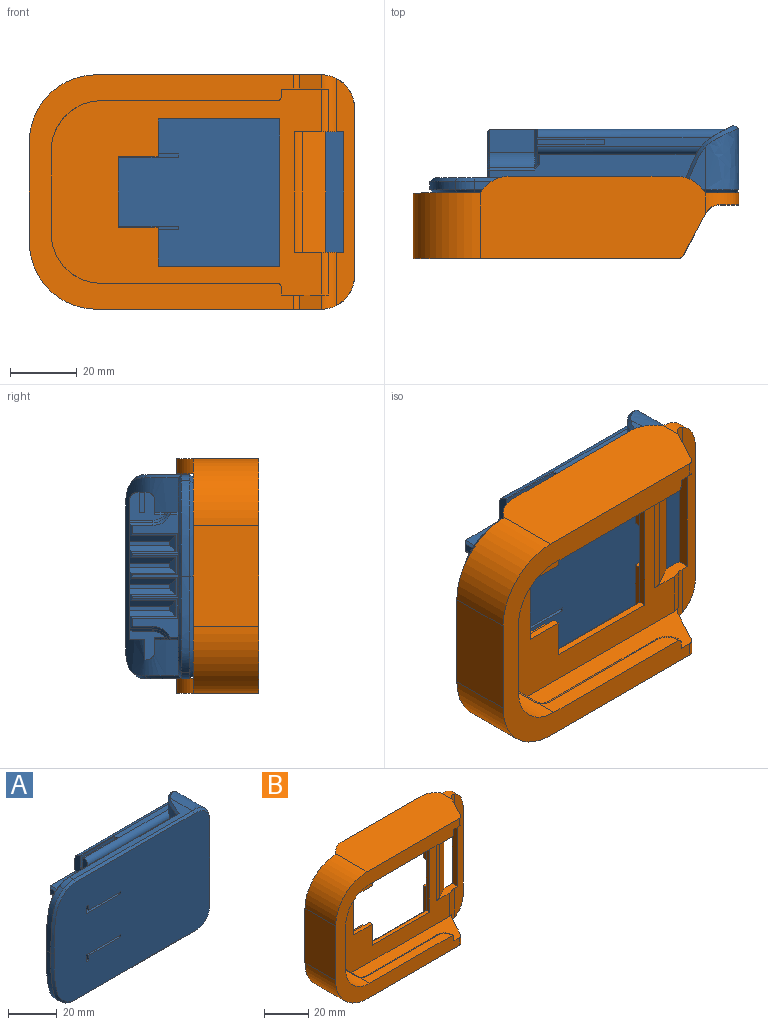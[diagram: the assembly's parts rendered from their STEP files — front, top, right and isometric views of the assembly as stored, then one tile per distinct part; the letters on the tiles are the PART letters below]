
ASSEMBLY  parts=2 mates=1
PART A: 135 faces, bbox 93.4x24.2x62.2 mm
  f0: plane 91.38x60.19mm, normal (0,-1,0), area 5145.7mm2, adj f1,f102,f103,f104,f105,f106,f107,f108
  f1: plane 18.5x16.5mm, normal (0,0,1), area 305.3mm2, adj f0,f122,f124,f134
  f2: plane 13x12mm, normal (0,0,1), area 37.3mm2, adj f6,f24,f25,f39,f122,f123
  f3: plane 61.69x7.04mm, normal (0,0,-1), area 352.6mm2, adj f8,f15,f19,f85,f86,f88,f99
  f4: plane 61.69x7.04mm, normal (0,0,1), area 352.6mm2, adj f9,f15,f18,f69,f72,f75,f99
  f5: plane 49.52x0.5mm, normal (0,0,-1), area 24.6mm2, adj f10,f12,f55,f99
  f6: plane 70.51x41.5mm, normal (0,1,0), area 2710mm2, adj f2,f11,f14,f23,f24,f26,f27,f28
  f7: plane 51.92x2.54mm, normal (0,0,1), area 95.9mm2, adj f13,f14,f20,f22,f50,f53,f99
  f8: plane 47.42x4.25mm, normal (0,-1,0), area 166.2mm2, adj f3,f12,f55,f86,f99
  f9: plane 47.42x4.25mm, normal (0,-1,0), area 166.2mm2, adj f4,f13,f53,f69,f99
  f10: plane 49.51x6mm, normal (0,1,0), area 297.1mm2, adj f5,f11,f55,f99
  f11: plane 56.3x4.58mm, normal (0,0,-1), area 236.2mm2, adj f6,f10,f55,f99
  f12: cylinder r=2.5mm len=49.08mm, axis (1,0,0), area 189.5mm2, adj f5,f8,f55,f99
  f13: cylinder r=2.5mm len=49.08mm, axis (-1,0,0), area 189.5mm2, adj f7,f9,f53,f99
  f14: cylinder r=2.5mm len=56.26mm, axis (-1,0,0), area 212.4mm2, adj f6,f7,f53,f99
  f15: plane 76.68x60.17mm, normal (0,1,0), area 2097.9mm2, adj f3,f4,f16,f18,f19,f99,f111,f112
  f16: plane 36.5x13.75mm, normal (-1,0,0), area 123.2mm2, adj f15,f18,f19,f57,f58,f59,f60,f61
  f17: plane 41x18.31mm, normal (1,0,0), area 750.7mm2, adj f100,f101,f102,f118
  f18: plane 2.37x0.75mm, normal (-0.71,0,0.71), area 2.5mm2, adj f4,f15,f16,f77
  f19: plane 2.37x0.75mm, normal (-0.71,0,-0.71), area 2.5mm2, adj f3,f15,f16,f82
  f20: plane 20x6mm, normal (0,-1,0), area 120mm2, adj f7,f21,f50,f53
  f21: plane 20x1.5mm, normal (0,0,1), area 30mm2, adj f20,f22,f50,f53
  f22: plane 20x6mm, normal (0,1,0), area 120mm2, adj f7,f21,f50,f53
  f23: plane 13x12mm, normal (0,0,-1), area 156mm2, adj f6,f24,f25,f38
  f24: plane 12x1.2mm, normal (-1,0,0), area 14.4mm2, adj f2,f6,f23,f25,f125
  f25: plane 13x1.2mm, normal (0,1,0), area 15.6mm2, adj f2,f23,f24,f40,f125
  f26: plane 13x12mm, normal (0,0,1), area 156mm2, adj f6,f28,f29,f42
  f27: plane 13x12mm, normal (0,0,-1), area 156mm2, adj f6,f28,f29,f41
  f28: plane 12x1.2mm, normal (-1,0,0), area 14.4mm2, adj f6,f26,f27,f29
  f29: plane 13x1.2mm, normal (0,1,0), area 15.6mm2, adj f26,f27,f28,f43
  f30: plane 13x12mm, normal (0,0,1), area 156mm2, adj f6,f32,f33,f45
  f31: plane 13x12mm, normal (0,0,-1), area 156mm2, adj f6,f32,f33,f44
  f32: plane 12x1.2mm, normal (-1,0,0), area 14.4mm2, adj f6,f30,f31,f33
  f33: plane 13x1.2mm, normal (0,1,0), area 15.6mm2, adj f30,f31,f32,f46
  f34: plane 13x12mm, normal (0,0,-1), area 37.3mm2, adj f6,f35,f37,f47,f127,f128
  f35: plane 12x1.2mm, normal (-1,0,0), area 14.4mm2, adj f6,f34,f36,f37,f126
  f36: plane 13x12mm, normal (0,0,1), area 156mm2, adj f6,f35,f37,f48
  f37: plane 13x1.2mm, normal (0,1,0), area 15.6mm2, adj f34,f35,f36,f49,f126
  f38: plane 13.78x1.78mm, normal (-0.71,0,-0.71), area 32.3mm2, adj f6,f23,f40,f76,f78
  f39: plane 13.78x1.78mm, normal (-0.71,0,0.71), area 32.3mm2, adj f2,f6,f40,f80,f81
  f40: plane 4.76x1.78mm, normal (-0.71,0.71,0), area 7.5mm2, adj f25,f38,f39,f79
  f41: plane 13.78x1.78mm, normal (-0.71,0,-0.71), area 32.3mm2, adj f6,f27,f43,f63,f66
  f42: plane 13.78x1.78mm, normal (-0.71,0,0.71), area 32.3mm2, adj f6,f26,f43,f73,f76
  f43: plane 4.76x1.78mm, normal (-0.71,0.71,0), area 7.5mm2, adj f29,f41,f42,f70
  f44: plane 13.78x1.78mm, normal (-0.71,0,-0.71), area 32.3mm2, adj f6,f31,f46,f57,f58
  f45: plane 13.78x1.78mm, normal (-0.71,0,0.71), area 32.3mm2, adj f6,f30,f46,f61,f63
  f46: plane 4.76x1.78mm, normal (-0.71,0.71,0), area 7.5mm2, adj f33,f44,f45,f59
  f47: plane 13.78x1.78mm, normal (-0.71,0,-0.71), area 32.3mm2, adj f6,f34,f49,f64,f67
  f48: plane 13.78x1.78mm, normal (-0.71,0,0.71), area 32.3mm2, adj f6,f36,f49,f58,f60
  f49: plane 4.76x1.78mm, normal (-0.71,0.71,0), area 7.5mm2, adj f37,f47,f48,f62
  f50: plane 6x1.5mm, normal (-1,0,0), area 9mm2, adj f7,f20,f21,f22
  f51: cylinder r=5mm len=13.5mm, axis (-1,0,0), area 74.4mm2, adj f52,f68,f74,f75
  f52: plane 13.5x7mm, normal (0,0,1), area 94.5mm2, adj f6,f51,f65,f71
  f53: plane 10.36x8.4mm, normal (-1,0,0), area 54.4mm2, adj f6,f7,f9,f13,f14,f20,f21,f22
  f54: cylinder r=5mm len=13.5mm, axis (-1,0,0), area 74.2mm2, adj f84,f85,f89,f90
  f55: plane 10.36x8.57mm, normal (-1,0,0), area 38.3mm2, adj f5,f6,f8,f10,f11,f12,f86,f90
  f56: plane 13.5x6.99mm, normal (0,0.02,-1), area 94.4mm2, adj f6,f83,f89,f92
  f57: plane 13.78x0.53mm, normal (-0.92,0,-0.38), area 7.7mm2, adj f16,f44,f58,f59
  f58: plane 2.8x0.75mm, normal (-0.71,0.71,0), area 2.1mm2, adj f6,f16,f44,f48,f57,f60
  f59: plane 5.82x0.53mm, normal (-0.92,0.38,0), area 3mm2, adj f16,f46,f57,f61
  f60: plane 13.78x0.53mm, normal (-0.92,0,0.38), area 7.7mm2, adj f16,f48,f58,f62
  f61: plane 13.78x0.53mm, normal (-0.92,0,0.38), area 7.7mm2, adj f16,f45,f59,f63
  f62: plane 5.82x0.53mm, normal (-0.92,0.38,0), area 3mm2, adj f16,f49,f60,f64
  f63: plane 2.8x0.75mm, normal (-0.71,0.71,0), area 2.1mm2, adj f6,f16,f41,f45,f61,f66
  f64: plane 13.78x0.53mm, normal (-0.92,0,-0.38), area 7.7mm2, adj f16,f47,f62,f67
  f65: plane 7x0.75mm, normal (-0.71,0,0.71), area 7.4mm2, adj f6,f52,f53,f68
  f66: plane 13.78x0.53mm, normal (-0.92,0,-0.38), area 7.7mm2, adj f16,f41,f63,f70
  f67: plane 4.25x0.75mm, normal (-0.71,0.71,0), area 3.7mm2, adj f6,f16,f47,f64,f71
  f68: cone r=4.25mm half-angle=45deg, axis (-1,0,0), area 5mm2, adj f51,f53,f65,f72
  f69: plane 2.86x0.75mm, normal (-0.71,0,0.71), area 3mm2, adj f4,f9,f53,f72
  f70: plane 5.82x0.53mm, normal (-0.92,0.38,0), area 3mm2, adj f16,f43,f66,f73
  f71: plane 7x0.75mm, normal (-0.71,0,0.71), area 7mm2, adj f16,f52,f67,f74
  f72: bspline ~1.77x1.5mm, area 1.4mm2, adj f4,f68,f69,f75
  f73: plane 13.78x0.53mm, normal (-0.92,0,0.38), area 7.7mm2, adj f16,f42,f70,f76
  f74: cone r=5mm half-angle=45deg, axis (-1,0,0), area 6.3mm2, adj f16,f51,f71,f77
  f75: plane 13.5x0.67mm, normal (0,0.52,0.85), area 10.6mm2, adj f4,f51,f72,f77
  f76: plane 2.8x0.75mm, normal (-0.71,0.71,0), area 2.1mm2, adj f6,f16,f38,f42,f73,f78
  f77: plane 0.75x0.75mm, normal (-0.65,0.4,0.65), area 0.4mm2, adj f18,f74,f75
  f78: plane 13.78x0.53mm, normal (-0.92,0,-0.38), area 7.7mm2, adj f16,f38,f76,f79
  f79: plane 5.82x0.53mm, normal (-0.92,0.38,0), area 3mm2, adj f16,f40,f78,f80
  f80: plane 13.78x0.53mm, normal (-0.92,0,0.38), area 7.7mm2, adj f16,f39,f79,f81
  f81: plane 4.08x0.75mm, normal (-0.71,0.71,0), area 3.5mm2, adj f6,f16,f39,f80,f83
  f82: plane 0.75x0.75mm, normal (-0.65,0.4,-0.65), area 0.4mm2, adj f19,f84,f85
  f83: plane 7.01x0.91mm, normal (-0.71,0.02,-0.71), area 7mm2, adj f16,f56,f81,f87
  f84: cone r=5.75mm half-angle=45deg, axis (-1,0,0), area 6.3mm2, adj f16,f54,f82,f87
  f85: plane 13.5x0.67mm, normal (0,0.52,-0.85), area 10.6mm2, adj f3,f54,f82,f88
  f86: plane 2.86x0.75mm, normal (-0.71,0,-0.71), area 3mm2, adj f3,f8,f55,f88
  f87: plane 0.75x0.75mm, normal (-0.71,0.01,-0.71), area 0mm2, adj f83,f84,f89
  f88: bspline ~1.77x1.5mm, area 1.4mm2, adj f3,f85,f86,f90
  f89: plane 13.5x0.02mm, normal (0,0.01,-1), area 0.2mm2, adj f54,f56,f87,f91
  f90: cone r=5mm half-angle=45deg, axis (-1,0,0), area 4.9mm2, adj f54,f55,f88,f91
  f91: plane 0.75x0.75mm, normal (-0.71,0.01,-0.71), area 0mm2, adj f55,f89,f90,f92
  f92: plane 6.99x0.92mm, normal (-0.71,0.02,-0.71), area 7.4mm2, adj f6,f55,f56,f91
  f93: plane 69.47x13.29mm, normal (0,0,1), area 200.8mm2, adj f97,f101,f106,f112,f114
  f94: extruded ~28.63x7.5mm, area 77.3mm2, adj f95,f97,f110,f113
  f95: extruded ~28.63x7.5mm, area 77.3mm2, adj f94,f98,f109,f115
  f96: plane 69.47x13.29mm, normal (0,0,-1), area 200.8mm2, adj f98,f100,f105,f119,f121
  f97: cylinder r=10mm len=5.83mm, axis (0,1,0), area 15.6mm2, adj f93,f94,f108,f111
  f98: cylinder r=10mm len=5.83mm, axis (0,1,0), area 15.6mm2, adj f95,f96,f107,f117
  f99: extruded ~59x15.71mm, area 451mm2, adj f3,f4,f5,f6,f7,f8,f9,f10
  f100: bspline ~23.01x10mm, area 251.8mm2, adj f17,f96,f103,f120
  f101: bspline ~23.01x10mm, area 251.8mm2, adj f17,f93,f104,f116
  f102: plane 41x1mm, normal (0.71,-0.71,0), area 58mm2, adj f0,f17,f103,f104
  f103: bspline ~10.01x10mm, area 21.9mm2, adj f0,f100,f102,f105
  f104: bspline ~10.01x10mm, area 21.9mm2, adj f0,f101,f102,f106
  f105: plane 68.84x1mm, normal (0,-0.71,-0.71), area 97.3mm2, adj f0,f96,f103,f107
  f106: plane 68.84x1mm, normal (0,-0.71,0.71), area 97.3mm2, adj f0,f93,f104,f108
  f107: cone r=9mm half-angle=45deg, axis (0,1,0), area 8.4mm2, adj f0,f98,f105,f109
  f108: cone r=9mm half-angle=45deg, axis (0,1,0), area 8.4mm2, adj f0,f97,f106,f110
  f109: bspline ~30.14x8.1mm, area 43mm2, adj f0,f95,f107,f110
  f110: bspline ~30.14x8.1mm, area 43mm2, adj f0,f94,f108,f109
  f111: cone r=9mm half-angle=45deg, axis (0,-1,0), area 8.4mm2, adj f15,f97,f112,f113
  f112: plane 63.82x1.01mm, normal (0,0.71,0.71), area 89.8mm2, adj f15,f93,f111,f114
  f113: bspline ~30.14x8.1mm, area 43mm2, adj f15,f94,f111,f115
  f114: bspline ~10.83x5.94mm, area 15.9mm2, adj f93,f99,f112,f116
  f115: bspline ~30.14x8.1mm, area 43mm2, adj f15,f95,f113,f117
  f116: bspline ~10.75x10mm, area 27.1mm2, adj f99,f101,f114,f118
  f117: cone r=9mm half-angle=45deg, axis (0,-1,0), area 8.4mm2, adj f15,f98,f115,f119
  f118: plane 41x1.44mm, normal (0.53,0.85,0), area 69.7mm2, adj f17,f99,f116,f120
  f119: plane 63.82x1.01mm, normal (0,0.71,-0.71), area 89.8mm2, adj f15,f96,f117,f121
  f120: bspline ~10.75x10mm, area 27.1mm2, adj f99,f100,f118,f121
  f121: bspline ~11.34x6.17mm, area 15.9mm2, adj f96,f99,f119,f120
  f122: plane 20x3.5mm, normal (0,-1,0), area 23.8mm2, adj f1,f2,f123,f124,f125,f133,f134
  f123: plane 16.5x3.5mm, normal (1,0,0), area 57.8mm2, adj f0,f2,f122,f125,f133
  f124: plane 16.5x1mm, normal (-1,0,0), area 16.5mm2, adj f0,f1,f122,f125
  f125: plane 20x16.5mm, normal (0,0,-1), area 211.2mm2, adj f0,f24,f25,f122,f123,f124
  f126: plane 20x16.5mm, normal (0,0,1), area 211.3mm2, adj f0,f35,f37,f127,f128,f129
  f127: plane 16.5x3.5mm, normal (1,0,0), area 57.7mm2, adj f0,f34,f126,f128,f131
  f128: plane 20x3.5mm, normal (0,-1,0), area 23.7mm2, adj f34,f126,f127,f129,f130,f131,f132
  f129: plane 16.5x1mm, normal (-1,0,0), area 16.5mm2, adj f0,f126,f128,f130
  f130: plane 18.5x16.5mm, normal (0,0,-1), area 305.2mm2, adj f0,f128,f129,f132
  f131: plane 16.5x1.5mm, normal (0,0,-1), area 24.7mm2, adj f0,f127,f128,f132
  f132: plane 16.5x2.5mm, normal (-1,0,0), area 41.3mm2, adj f0,f128,f130,f131
  f133: plane 16.5x1.5mm, normal (0,0,1), area 24.7mm2, adj f0,f122,f123,f134
  f134: plane 16.5x2.5mm, normal (-1,0,0), area 41.2mm2, adj f0,f1,f122,f133
PART B: 83 faces, bbox 97.1x24.5x70 mm
  f0: plane 29.99x19.5mm, normal (-1,0,0), area 584.8mm2, adj f1,f4,f9,f44
  f1: cylinder r=20mm len=20mm, axis (0,-1,0), area 612.6mm2, adj f0,f4,f9,f10
  f2: plane 14.8x4.5mm, normal (0,0,1), area 38.3mm2, adj f3,f4,f6,f54,f55,f58,f61,f74
  f3: plane 80.77x61.5mm, normal (0,-1,0), area 2617.9mm2, adj f2,f7,f8,f27,f28,f29,f30,f31
  f4: plane 97.09x69.99mm, normal (0,1,0), area 3587.8mm2, adj f0,f1,f2,f12,f13,f14,f15,f16
  f5: plane 12.29x6.56mm, normal (0.88,-0.47,0), area 59.2mm2, adj f8,f11,f13,f52,f59
  f6: plane 67.82x5.47mm, normal (0,-1,0), area 263.1mm2, adj f2,f12,f13,f14,f53,f54,f58,f59
  f7: plane 67.27x15.51mm, normal (0,0,1), area 626.1mm2, adj f3,f9,f40,f41,f43,f47,f48,f50
  f8: plane 67.31x15.5mm, normal (0,0,-1), area 626.6mm2, adj f3,f5,f9,f36,f37,f39,f46,f49
  f9: plane 78.89x69.99mm, normal (0,-1,0), area 1474.1mm2, adj f0,f1,f7,f8,f10,f11,f37,f38
  f10: plane 67.09x24.5mm, normal (0,0,-1), area 1572.3mm2, adj f1,f9,f12,f50,f51,f78,f79,f80
  f11: plane 67.09x24.5mm, normal (0,0,1), area 1572.3mm2, adj f5,f9,f13,f44,f52,f76,f81,f82
  f12: cylinder r=10mm len=10mm, axis (0,1,0), area 58.7mm2, adj f4,f6,f10,f14,f50,f58
  f13: cylinder r=10mm len=10mm, axis (0,-1,0), area 58.7mm2, adj f4,f5,f6,f11,f14,f59
  f14: plane 49.99x3.5mm, normal (1,0,0), area 175mm2, adj f4,f6,f12,f13
  f15: plane 19.05x2.5mm, normal (-1,0,0), area 47.6mm2, adj f4,f16,f26,f35
  f16: plane 2.5x1.78mm, normal (0,0,-1), area 4.4mm2, adj f4,f15,f17,f35
  f17: plane 15.24x2.5mm, normal (-1,0,0), area 38.1mm2, adj f4,f16,f18,f35
  f18: plane 2.5x1.78mm, normal (0,0,1), area 4.4mm2, adj f4,f17,f19,f35
  f19: plane 14.48x2.5mm, normal (-1,0,0), area 36.2mm2, adj f4,f18,f20,f35
  f20: plane 38.35x2.5mm, normal (0,0,1), area 95.9mm2, adj f4,f19,f21,f35
  f21: plane 12.07x2.5mm, normal (1,0,0), area 30.2mm2, adj f4,f20,f22,f35
  f22: plane 12.07x2.5mm, normal (0,0,1), area 30.2mm2, adj f4,f21,f23,f35
  f23: plane 24.64x2.5mm, normal (1,0,0), area 61.6mm2, adj f4,f22,f24,f35
  f24: plane 12.07x2.5mm, normal (0,0,-1), area 30.2mm2, adj f4,f23,f25,f35
  f25: plane 12.07x2.5mm, normal (1,0,0), area 30.2mm2, adj f4,f24,f26,f35
  f26: plane 38.35x2.5mm, normal (0,0,-1), area 95.9mm2, adj f4,f15,f25,f35
  f27: plane 21.08x2mm, normal (1,0,0), area 42.2mm2, adj f3,f28,f34,f35
  f28: plane 11.94x2mm, normal (0,0,-1), area 23.9mm2, adj f3,f27,f29,f35
  f29: plane 11.26x2mm, normal (1,0,0), area 22.5mm2, adj f3,f28,f30,f35
  f30: plane 36.32x2mm, normal (0,0,-1), area 72.6mm2, adj f3,f29,f31,f35
  f31: plane 43.94x2mm, normal (-1,0,0), area 87.9mm2, adj f3,f30,f32,f35
  f32: plane 36.32x2mm, normal (0,0,1), area 72.6mm2, adj f3,f31,f33,f35
  f33: plane 11.6x2mm, normal (1,0,0), area 23.2mm2, adj f3,f32,f34,f35
  f34: plane 11.94x2mm, normal (0,0,1), area 23.9mm2, adj f3,f27,f33,f35
  f35: plane 52.2x48.77mm, normal (0,1,0), area 347.1mm2, adj f15,f16,f17,f18,f19,f20,f21,f22
  f36: plane 46x2.5mm, normal (0,1,0), area 115mm2, adj f8,f39,f49,f64
  f37: plane 2.5x0.8mm, normal (1,0,0), area 2mm2, adj f8,f9,f39,f62
  f38: plane 52.64x6.38mm, normal (0,0,-1), area 250.4mm2, adj f9,f56,f62,f63,f64,f65
  f39: cylinder r=5mm len=5mm, axis (0,0,-1), area 19.6mm2, adj f8,f36,f37,f63
  f40: plane 45.95x2.5mm, normal (0,1,0), area 114.8mm2, adj f7,f43,f48,f70
  f41: plane 2.5x0.8mm, normal (1,0,0), area 2mm2, adj f7,f9,f43,f68
  f42: plane 52.64x6.54mm, normal (0,0,1), area 250.6mm2, adj f9,f57,f68,f69,f70,f71
  f43: cylinder r=5mm len=5mm, axis (0,0,1), area 19.6mm2, adj f7,f40,f41,f69
  f44: cylinder r=20mm len=20mm, axis (0,-1,0), area 612.6mm2, adj f0,f4,f9,f11
  f45: plane 24.5x15mm, normal (1,0,0), area 367.5mm2, adj f3,f9,f56,f57
  f46: plane 7.2x2.5mm, normal (1,0,0), area 18mm2, adj f3,f8,f49,f67
  f47: plane 7.2x2.49mm, normal (1,0,-0.01), area 17.9mm2, adj f3,f7,f48,f73
  f48: cylinder r=2mm len=2.55mm, axis (0.01,0,1), area 7.8mm2, adj f7,f40,f47,f71,f72
  f49: cylinder r=2mm len=2.5mm, axis (0,0,-1), area 7.9mm2, adj f8,f36,f46,f65,f66
  f50: plane 12.29x6.56mm, normal (0.88,-0.47,0), area 59.1mm2, adj f7,f10,f12,f51,f58
  f51: cylinder r=2mm len=4.24mm, axis (0,0,-1), area 9.2mm2, adj f7,f9,f10,f50
  f52: cylinder r=2mm len=4.25mm, axis (0,0,-1), area 9.2mm2, adj f5,f8,f9,f11
  f53: plane 14.8x4.5mm, normal (0,0,-1), area 38.3mm2, adj f3,f4,f6,f54,f55,f59,f60,f74
  f54: plane 36x3.5mm, normal (-1,0,0), area 126mm2, adj f2,f4,f6,f53
  f55: plane 36x6.97mm, normal (0.49,-0.87,0), area 286.9mm2, adj f2,f4,f53,f74
  f56: cylinder r=15mm len=15mm, axis (0,1,0), area 350.7mm2, adj f3,f9,f38,f45,f66,f67
  f57: cylinder r=15mm len=15mm, axis (0,1,0), area 351.3mm2, adj f3,f9,f42,f45,f72,f73
  f58: cylinder r=5mm len=17mm, axis (0,0,-1), area 50mm2, adj f2,f6,f7,f12,f50,f61
  f59: cylinder r=5mm len=17mm, axis (0,0,-1), area 50mm2, adj f5,f6,f8,f13,f53,f60
  f60: cylinder r=5mm len=12.75mm, axis (0,0,-1), area 28.7mm2, adj f3,f8,f53,f59
  f61: cylinder r=5mm len=12.75mm, axis (0,0,-1), area 28.8mm2, adj f2,f3,f7,f58
  f62: cylinder r=1mm len=1mm, axis (0,1,0), area 1.3mm2, adj f9,f37,f38,f63
  f63: torus R=4mm, axis (0,0,-1), area 11.4mm2, adj f38,f39,f62,f64
  f64: cylinder r=1mm len=46mm, axis (-1,0,0), area 72.3mm2, adj f36,f38,f63,f65
  f65: torus R=3mm, axis (0,0,-1), area 4mm2, adj f38,f49,f64,f66
  f66: bspline ~2.65x1.47mm, area 1.8mm2, adj f49,f56,f65,f67
  f67: cylinder r=1mm len=7.2mm, axis (0,1,0), area 11.1mm2, adj f3,f46,f56,f66
  f68: cylinder r=1mm len=1mm, axis (0,-1,0), area 1.3mm2, adj f9,f41,f42,f69
  f69: torus R=4mm, axis (0,0,1), area 11.4mm2, adj f42,f43,f68,f70
  f70: cylinder r=1mm len=45.92mm, axis (1,0,0), area 72.1mm2, adj f40,f42,f69,f71
  f71: bspline ~2.72x2.16mm, area 4.2mm2, adj f42,f48,f70,f72
  f72: bspline ~2.09x1.22mm, area 1.6mm2, adj f48,f57,f71,f73
  f73: cylinder r=1mm len=7.2mm, axis (0,1,0), area 11.3mm2, adj f3,f47,f57,f72
  f74: cylinder r=5mm len=36mm, axis (0,0,1), area 91.3mm2, adj f2,f3,f53,f55
  f75: plane 67.09x5mm, normal (0,0,-1), area 310.3mm2, adj f4,f76,f81,f82
  f76: plane 49.77x4.5mm, normal (0,1,0), area 224mm2, adj f11,f75,f81,f82
  f77: plane 67.09x5mm, normal (0,0,1), area 310.3mm2, adj f4,f78,f79,f80
  f78: plane 49.77x4.5mm, normal (0,1,0), area 224mm2, adj f10,f77,f79,f80
  f79: cylinder r=10mm len=8.66mm, axis (0,0,-1), area 47.1mm2, adj f4,f10,f77,f78
  f80: cylinder r=10mm len=8.66mm, axis (0,0,-1), area 47.1mm2, adj f4,f10,f77,f78
  f81: cylinder r=10mm len=8.66mm, axis (0,0,1), area 47.1mm2, adj f4,f11,f75,f76
  f82: cylinder r=10mm len=8.66mm, axis (0,0,1), area 47.1mm2, adj f4,f11,f75,f76
PLACE A t=(1.59,-2.25,2.57)mm
PLACE B t=(21.7,-7.25,-0.23)mm
MATE planar B.f4 <-> A.f0  axis (0,1,0) through (3.98,-7.25,-0.21)mm
